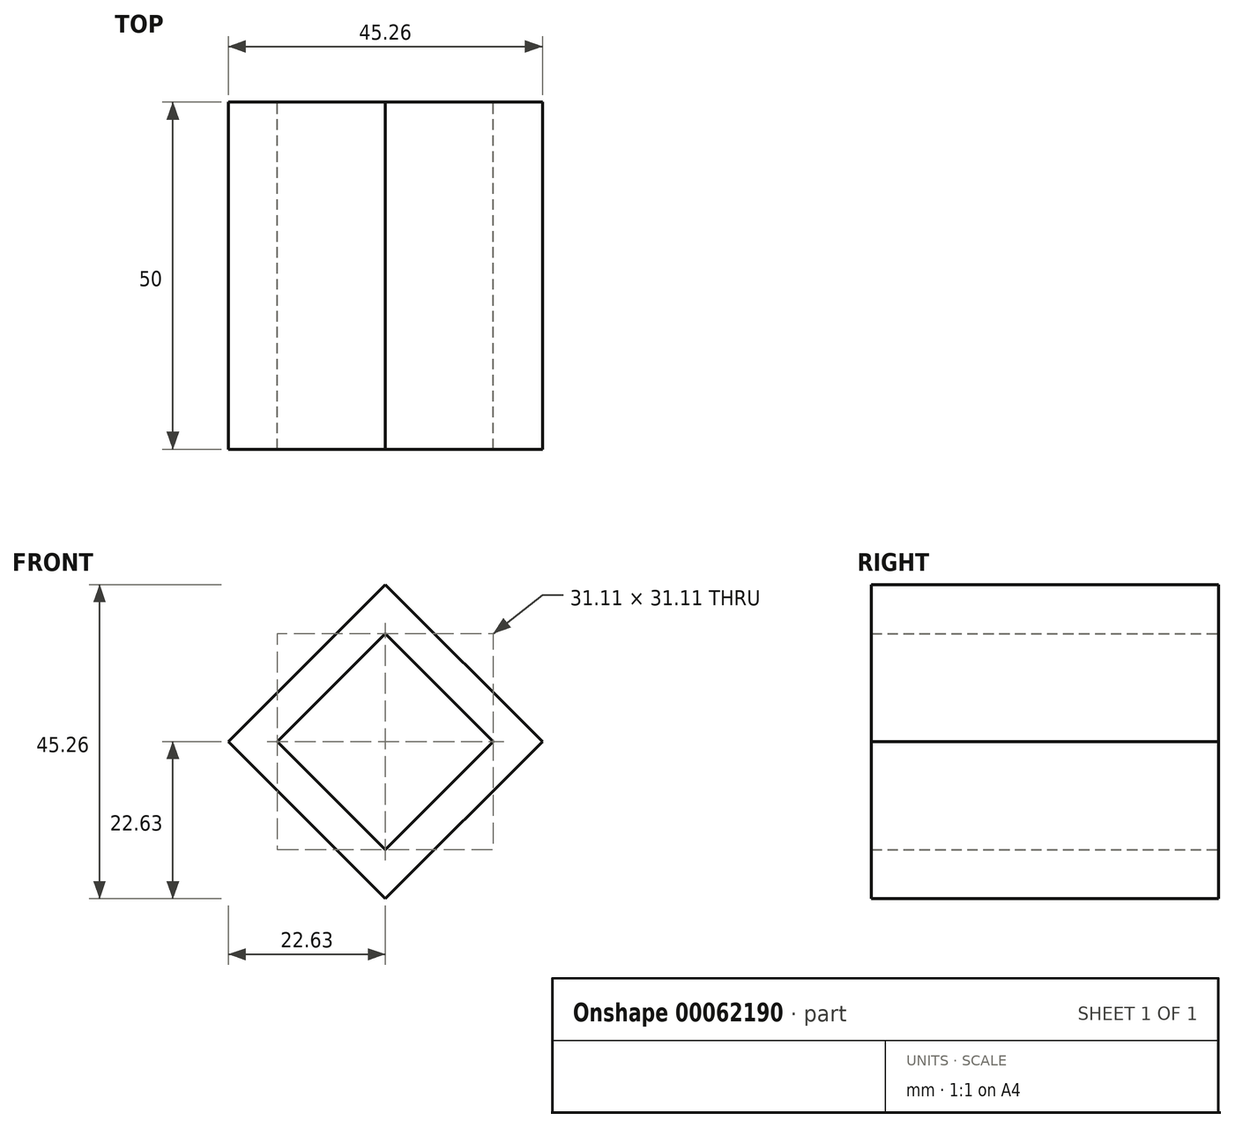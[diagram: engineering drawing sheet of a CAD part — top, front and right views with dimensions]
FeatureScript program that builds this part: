
annotation { "Feature Type Name" : "Feature", "Feature Type Description" : "" }
export const myFeature = defineFeature(function(context is Context, id is Id, definition is map)
    precondition{}
    {
        {
            var Q0;
            Q0=qCreatedBy(makeId("Front.planeOp"),FACE);
            var sketch = newSketch(context, id + "F0", { "sketchPlane" : qUnion([Q0])});
            skLineSegment(sketch, "E0", {"start": v(0, 15.56) * mm, "end": v(15.56, 0) * mm});
            skLineSegment(sketch, "E1", {"start": v(15.56, 0) * mm, "end": v(0, -15.56) * mm});
            skLineSegment(sketch, "E2", {"start": v(0, -15.56) * mm, "end": v(-15.56, 0) * mm});
            skLineSegment(sketch, "E3", {"start": v(-15.56, 0) * mm, "end": v(0, 15.56) * mm});
            skLineSegment(sketch, "E4.0", {"start": v(-22.63, 0) * mm, "end": v(0, 22.63) * mm});
            skLineSegment(sketch, "E4.1", {"start": v(0, -22.63) * mm, "end": v(-22.63, 0) * mm});
            skLineSegment(sketch, "E4.2", {"start": v(22.63, 0) * mm, "end": v(0, -22.63) * mm});
            skLineSegment(sketch, "E4.3", {"start": v(0, 22.63) * mm, "end": v(22.63, 0) * mm});
            skSolve(sketch);
        }
        {
            var Q0;
            Q0 = qSketchRegion(id + "F0", true);
            extrude(context, id + "F1", {"entities" : qUnion([Q0]), "depth" : 50 * mm});
        }
    });
